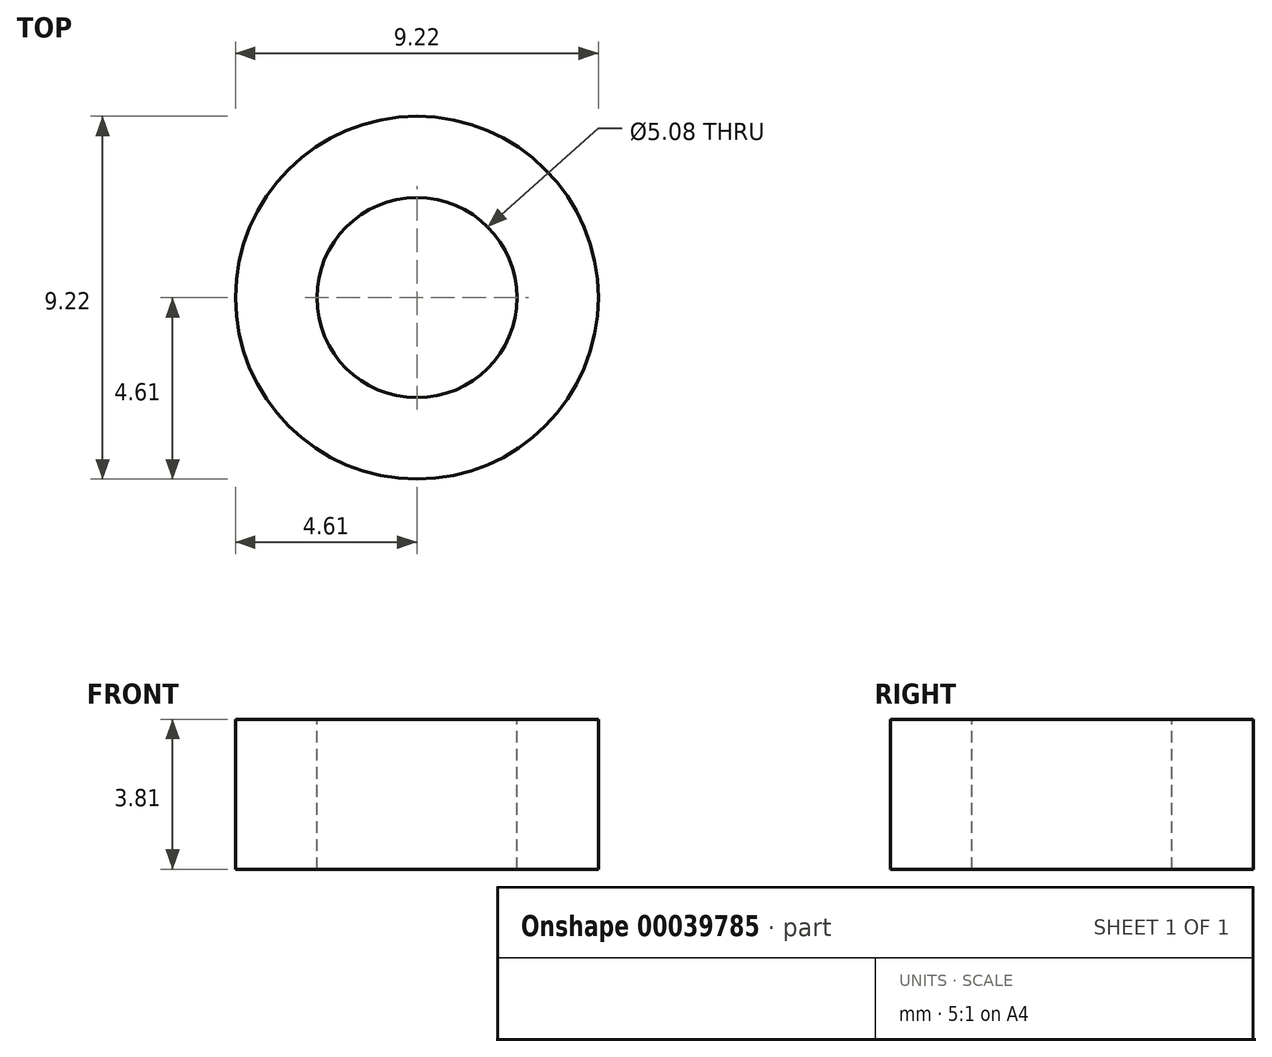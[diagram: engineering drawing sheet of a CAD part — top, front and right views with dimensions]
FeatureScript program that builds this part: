
annotation { "Feature Type Name" : "Feature", "Feature Type Description" : "" }
export const myFeature = defineFeature(function(context is Context, id is Id, definition is map)
    precondition{}
    {
        {
            var Q0;
            Q0=qCreatedBy(makeId("Top.planeOp"),FACE);
            var sketch = newSketch(context, id + "F0", { "sketchPlane" : qUnion([Q0])});
            skCircle(sketch, "E0", {"center": v(0, 0) * mm, "radius": 4.61 * mm});
            skLineSegment(sketch, "E1", {"start": v(-4.61, 0) * mm, "end": v(4.61, 0) * mm, "construction": true});
            skSolve(sketch);
        }
        {
            var Q0;
            Q0=makeQuery(id+"F0.imprint","IMPRINT",FACE,{"disambiguationData":[TD([[makeQuery(id+"F0.imprint","IMPRINT",EDGE,{"derivedFrom":sQuery(id+"F0.wireOp",EDGE,"E0")}),1.0]])]});
            extrude(context, id + "F1", {"entities" : qUnion([Q0]), "depth" : 3.8 * mm});
        }
        {
            var Q0;
            Q0=makeQuery(id+"F1.opExtrude","CAP_FACE",FACE,{"disambiguationData":[OSD([sQuery(id+"F0.wireOp",EDGE,"E0")])],"isStart":false});
            var sketch = newSketch(context, id + "F2", { "sketchPlane" : qUnion([Q0])});
            skCircle(sketch, "E2", {"center": v(0, 0) * mm, "radius": 2.54 * mm});
            skLineSegment(sketch, "E3", {"start": v(-2.54, 0) * mm, "end": v(2.54, 0) * mm, "construction": true});
            skSolve(sketch);
        }
        {
            var Q0;
            Q0 = qSketchRegion(id + "F2", true);
            extrude(context, id + "F3", {"entities" : qUnion([Q0]), "operationType" : NewBodyOperationType.REMOVE, "oppositeDirection" : true, "depth" : 127 * mm});
        }
    });
